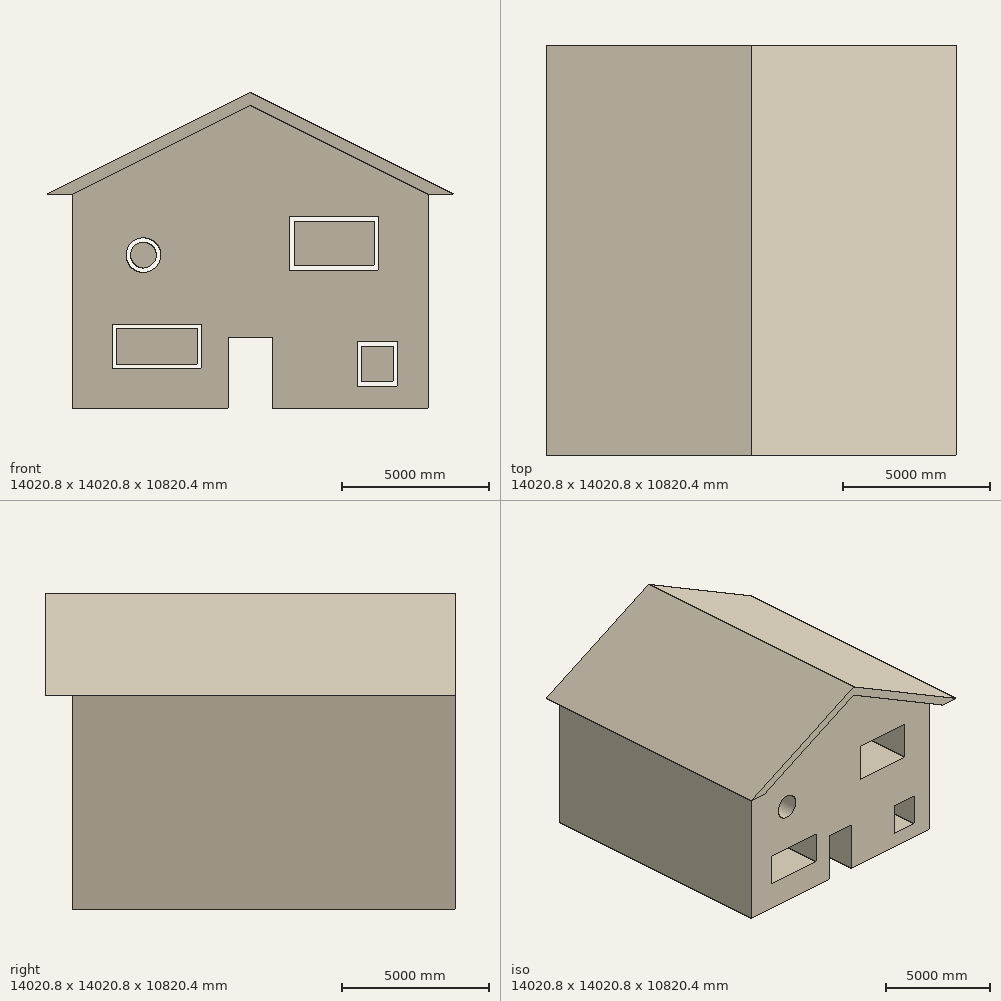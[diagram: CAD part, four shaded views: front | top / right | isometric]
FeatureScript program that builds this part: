
annotation { "Feature Type Name" : "Feature", "Feature Type Description" : "" }
export const myFeature = defineFeature(function(context is Context, id is Id, definition is map)
    precondition{}
    {
        {
            var Q0;
            Q0=qCreatedBy(makeId("Front.planeOp"),FACE);
            var sketch = newSketch(context, id + "F0", { "sketchPlane" : qUnion([Q0])});
            skLineSegment(sketch, "E0", {"start": v(0, 0) * mm, "end": v(-6096, 0) * mm});
            skLineSegment(sketch, "E1", {"start": v(0, 0) * mm, "end": v(6096, 0) * mm});
            skLineSegment(sketch, "E2", {"start": v(0, 0) * mm, "end": v(0, 3048) * mm, "construction": true});
            skLineSegment(sketch, "E3", {"start": v(0, 3048) * mm, "end": v(-6096, 0) * mm});
            skLineSegment(sketch, "E4", {"start": v(0, 3048) * mm, "end": v(6096, 0) * mm});
            skLineSegment(sketch, "E5", {"start": v(6096, 0) * mm, "end": v(7010.4, 0) * mm});
            skLineSegment(sketch, "E6", {"start": v(-6096, 0) * mm, "end": v(-7010.4, 0) * mm});
            skLineSegment(sketch, "E7", {"start": v(0, 3048) * mm, "end": v(0, 3505.2) * mm});
            skLineSegment(sketch, "E8", {"start": v(0, 3505.2) * mm, "end": v(-7010.4, 0) * mm});
            skLineSegment(sketch, "E9", {"start": v(0, 3505.2) * mm, "end": v(7010.4, 0) * mm});
            skLineSegment(sketch, "E10", {"start": v(-6096, 0) * mm, "end": v(-6096, -7315.2) * mm});
            skLineSegment(sketch, "E11", {"start": v(6096, 0) * mm, "end": v(6096, -7315.2) * mm});
            skLineSegment(sketch, "E12", {"start": v(-6096, -7315.2) * mm, "end": v(6096, -7315.2) * mm});
            skLineSegment(sketch, "E13", {"start": v(-6096, -7315.2) * mm, "end": v(-6096, -7620) * mm});
            skLineSegment(sketch, "E14", {"start": v(-6096, -7620) * mm, "end": v(6096, -7620) * mm});
            skLineSegment(sketch, "E15", {"start": v(6096, -7315.2) * mm, "end": v(6096, -7620) * mm});
            skLineSegment(sketch, "E16", {"start": v(0, -7315.2) * mm, "end": v(-457.2, -7315.2) * mm});
            skLineSegment(sketch, "E17", {"start": v(-457.2, -7315.2) * mm, "end": v(-457.2, -5181.6) * mm});
            skLineSegment(sketch, "E18", {"start": v(-457.2, -5181.6) * mm, "end": v(457.2, -5181.6) * mm});
            skLineSegment(sketch, "E19", {"start": v(457.2, -5181.6) * mm, "end": v(457.2, -7315.2) * mm});
            skLineSegment(sketch, "E20.bottom", {"start": v(-4572, -4572) * mm, "end": v(-1828.8, -4572) * mm});
            skLineSegment(sketch, "E20.top", {"start": v(-4572, -5791.2) * mm, "end": v(-1828.8, -5791.2) * mm});
            skLineSegment(sketch, "E20.left", {"start": v(-4572, -4572) * mm, "end": v(-4572, -5791.2) * mm});
            skLineSegment(sketch, "E20.right", {"start": v(-1828.8, -4572) * mm, "end": v(-1828.8, -5791.2) * mm});
            skLineSegment(sketch, "E21.0", {"start": v(-4724.4, -4419.6) * mm, "end": v(-1676.4, -4419.6) * mm});
            skLineSegment(sketch, "E21.1", {"start": v(-4724.4, -4419.6) * mm, "end": v(-4724.4, -5943.6) * mm});
            skLineSegment(sketch, "E21.2", {"start": v(-4724.4, -5943.6) * mm, "end": v(-1676.4, -5943.6) * mm});
            skLineSegment(sketch, "E21.3", {"start": v(-1676.4, -4419.6) * mm, "end": v(-1676.4, -5943.6) * mm});
            skLineSegment(sketch, "E22.bottom", {"start": v(3810, -5181.6) * mm, "end": v(4876.8, -5181.6) * mm});
            skLineSegment(sketch, "E22.top", {"start": v(3810, -6400.8) * mm, "end": v(4876.8, -6400.8) * mm});
            skLineSegment(sketch, "E22.left", {"start": v(3810, -5181.6) * mm, "end": v(3810, -6400.8) * mm});
            skLineSegment(sketch, "E22.right", {"start": v(4876.8, -5181.6) * mm, "end": v(4876.8, -6400.8) * mm});
            skLineSegment(sketch, "E23.0", {"start": v(3657.6, -5029.2) * mm, "end": v(5029.2, -5029.2) * mm});
            skLineSegment(sketch, "E23.1", {"start": v(3657.6, -5029.2) * mm, "end": v(3657.6, -6553.2) * mm});
            skLineSegment(sketch, "E23.2", {"start": v(3657.6, -6553.2) * mm, "end": v(5029.2, -6553.2) * mm});
            skLineSegment(sketch, "E23.3", {"start": v(5029.2, -5029.2) * mm, "end": v(5029.2, -6553.2) * mm});
            skLineSegment(sketch, "E24.0", {"start": v(762, -4876.8) * mm, "end": v(762, -7315.2) * mm});
            skLineSegment(sketch, "E24.1", {"start": v(-762, -4876.8) * mm, "end": v(762, -4876.8) * mm});
            skLineSegment(sketch, "E24.2", {"start": v(-762, -7315.2) * mm, "end": v(-762, -4876.8) * mm});
            skCircle(sketch, "E25", {"center": v(-3657.6, -2066.15) * mm, "radius": 592.52 * mm});
            skCircle(sketch, "E26.0", {"center": v(-3657.6, -2066.15) * mm, "radius": 440.12 * mm});
            skLineSegment(sketch, "E27.bottom", {"start": v(1490.3, -903.54) * mm, "end": v(4233.5, -903.54) * mm});
            skLineSegment(sketch, "E27.top", {"start": v(1490.3, -2427.54) * mm, "end": v(4233.5, -2427.54) * mm});
            skLineSegment(sketch, "E27.left", {"start": v(1490.3, -903.54) * mm, "end": v(1490.3, -2427.54) * mm});
            skLineSegment(sketch, "E27.right", {"start": v(4233.5, -903.54) * mm, "end": v(4233.5, -2427.54) * mm});
            skLineSegment(sketch, "E28.0", {"start": v(1337.9, -751.14) * mm, "end": v(4385.9, -751.14) * mm});
            skLineSegment(sketch, "E28.1", {"start": v(1337.9, -751.14) * mm, "end": v(1337.9, -2579.94) * mm});
            skLineSegment(sketch, "E28.2", {"start": v(1337.9, -2579.94) * mm, "end": v(4385.9, -2579.94) * mm});
            skLineSegment(sketch, "E28.3", {"start": v(4385.9, -751.14) * mm, "end": v(4385.9, -2579.94) * mm});
            skSolve(sketch);
        }
        {
            var Q0;
            Q0=makeQuery(id+"F0.imprint","IMPRINT",FACE,{"disambiguationData":[TD([[makeQuery(id+"F0.imprint","IMPRINT",EDGE,{"derivedFrom":sQuery(id+"F0.wireOp",EDGE,"E3")}),-1.0]])]});
            var Q1;
            Q1=makeQuery(id+"F0.imprint","IMPRINT",FACE,{"disambiguationData":[TD([[makeQuery(id+"F0.imprint","IMPRINT",EDGE,{"derivedFrom":sQuery(id+"F0.wireOp",EDGE,"E4")}),1.0]])]});
            extrude(context, id + "F1", {"entities" : qUnion([Q0, Q1]), "depth" : 14020.8 * mm, "offsetDistance" : 30.48 * mm});
        }
        {
            var Q0;
            Q0=makeQuery(id+"F0.imprint","IMPRINT",FACE,{"disambiguationData":[TD([[makeQuery(id+"F0.imprint","IMPRINT",EDGE,{"derivedFrom":sQuery(id+"F0.wireOp",EDGE,"E0")}),-1.0]])]});
            extrude(context, id + "F2", {"entities" : qUnion([Q0]), "operationType" : NewBodyOperationType.ADD, "depth" : 13106.4 * mm, "offsetDistance" : 30.48 * mm});
        }
        {
            var Q0;
            Q0=makeQuery(id+"F0.imprint","IMPRINT",FACE,{"disambiguationData":[TD([[makeQuery(id+"F0.imprint","IMPRINT",EDGE,{"derivedFrom":sQuery(id+"F0.wireOp",EDGE,"E0")}),-1.0]])]});
            extrude(context, id + "F3", {"entities" : qUnion([Q0]), "operationType" : NewBodyOperationType.ADD, "depth" : 914.4 * mm, "offsetDistance" : 30.48 * mm});
        }
        {
            var Q0;
            Q0=makeQuery(id+"F0.imprint","IMPRINT",FACE,{"disambiguationData":[TD([[makeQuery(id+"F0.imprint","IMPRINT",EDGE,{"derivedFrom":sQuery(id+"F0.wireOp",EDGE,"E0")}),1.0]])]});
            extrude(context, id + "F4", {"entities" : qUnion([Q0]), "operationType" : NewBodyOperationType.ADD, "depth" : 13106.4 * mm, "offsetDistance" : 30.48 * mm});
        }
        {
            var Q0;
            Q0=makeQuery(id+"F0.imprint","IMPRINT",FACE,{"disambiguationData":[TD([[makeQuery(id+"F0.imprint","IMPRINT",EDGE,{"derivedFrom":sQuery(id+"F0.wireOp",EDGE,"E3")}),-1.0]])]});
            var Q1;
            Q1=makeQuery(id+"F0.imprint","IMPRINT",FACE,{"disambiguationData":[TD([[makeQuery(id+"F0.imprint","IMPRINT",EDGE,{"derivedFrom":sQuery(id+"F0.wireOp",EDGE,"E4")}),1.0]])]});
            extrude(context, id + "F5", {"entities" : qUnion([Q0, Q1]), "operationType" : NewBodyOperationType.ADD, "depth" : 914.4 * mm, "offsetDistance" : 30.48 * mm});
        }
        {
            var Q0;
            Q0=makeQuery(id+"F0.imprint","IMPRINT",FACE,{"disambiguationData":[TD([[makeQuery(id+"F0.imprint","IMPRINT",EDGE,{"derivedFrom":sQuery(id+"F0.wireOp",EDGE,"E22.bottom")}),-1.0]])]});
            var Q1;
            Q1=makeQuery(id+"F0.imprint","IMPRINT",FACE,{"disambiguationData":[TD([[makeQuery(id+"F0.imprint","IMPRINT",EDGE,{"derivedFrom":sQuery(id+"F0.wireOp",EDGE,"E27.bottom")}),-1.0]])]});
            var Q2;
            Q2=makeQuery(id+"F0.imprint","IMPRINT",FACE,{"disambiguationData":[TD([[makeQuery(id+"F0.imprint","IMPRINT",EDGE,{"derivedFrom":sQuery(id+"F0.wireOp",EDGE,"E26.0")}),1.0]])]});
            var Q3;
            Q3=makeQuery(id+"F0.imprint","IMPRINT",FACE,{"disambiguationData":[TD([[makeQuery(id+"F0.imprint","IMPRINT",EDGE,{"derivedFrom":sQuery(id+"F0.wireOp",EDGE,"E20.bottom")}),-1.0]])]});
            extrude(context, id + "F6", {"entities" : qUnion([Q0, Q1, Q2, Q3]), "depth" : 1524 * mm, "offsetDistance" : 30.48 * mm});
        }
    });
